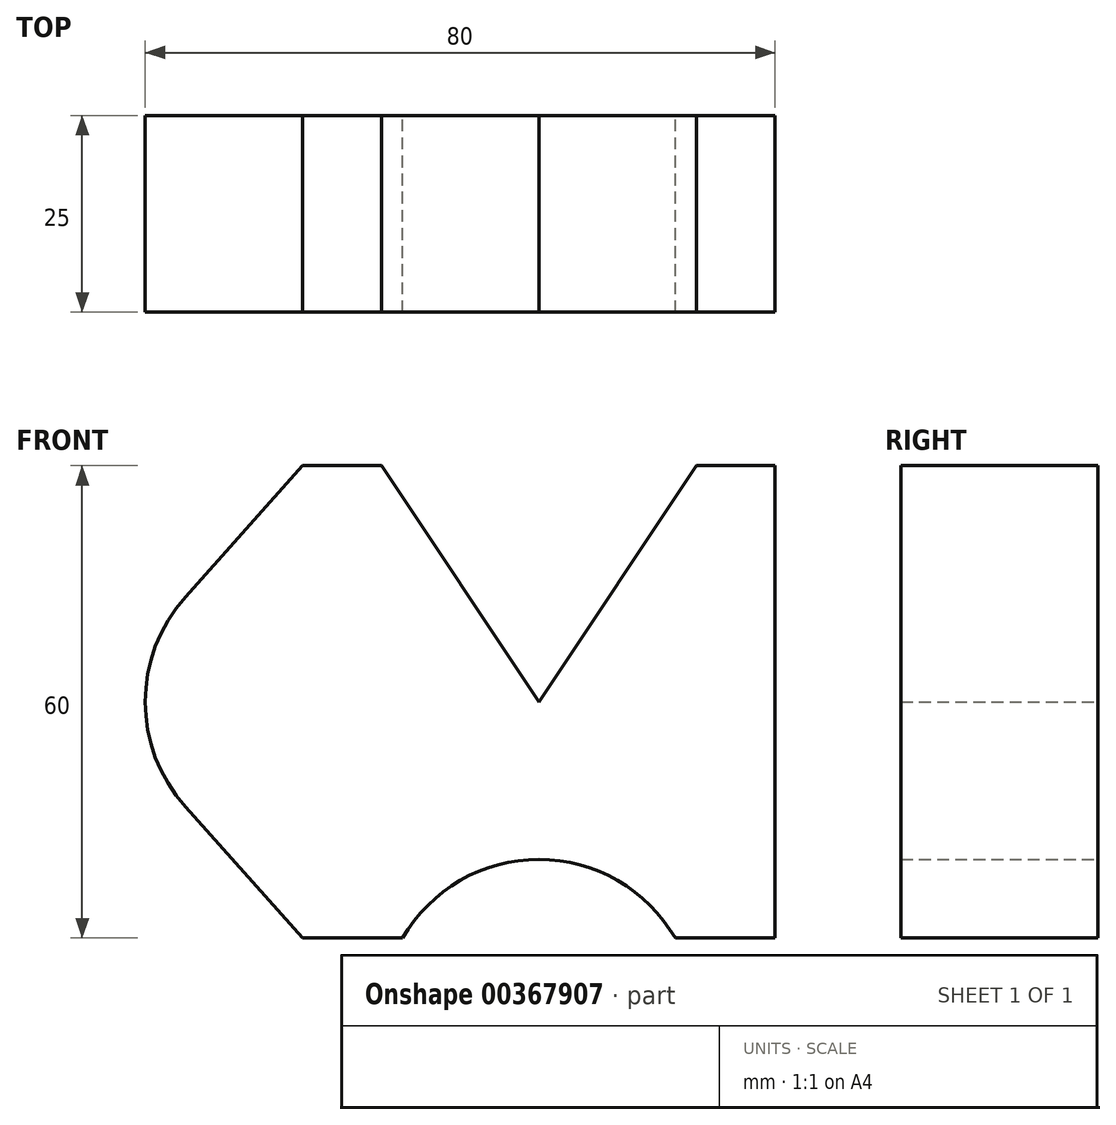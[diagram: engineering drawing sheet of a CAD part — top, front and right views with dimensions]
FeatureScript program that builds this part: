
annotation { "Feature Type Name" : "Feature", "Feature Type Description" : "" }
export const myFeature = defineFeature(function(context is Context, id is Id, definition is map)
    precondition{}
    {
        {
            var Q0;
            Q0=qCreatedBy(makeId("Front.planeOp"),FACE);
            var sketch = newSketch(context, id + "F0", { "sketchPlane" : qUnion([Q0])});
            skLineSegment(sketch, "E0", {"start": v(0, 0) * mm, "end": v(20, 30) * mm});
            skLineSegment(sketch, "E1", {"start": v(20, 30) * mm, "end": v(30, 30) * mm});
            skLineSegment(sketch, "E2", {"start": v(30, 30) * mm, "end": v(30, -30) * mm});
            skLineSegment(sketch, "E3", {"start": v(30, -30) * mm, "end": v(17.32, -30) * mm});
            skArc(sketch, "E4", {"start": v(17.32, -30) * mm, "mid": v(0, -20) * mm, "end": v(-17.32, -30) * mm});
            skLineSegment(sketch, "E5", {"start": v(-30, 30) * mm, "end": v(-20, 30) * mm});
            skLineSegment(sketch, "E6", {"start": v(-20, 30) * mm, "end": v(0, 0) * mm});
            skLineSegment(sketch, "E7", {"start": v(-17.32, -30) * mm, "end": v(-30, -30) * mm});
            skLineSegment(sketch, "E8", {"start": v(-30, -30) * mm, "end": v(-44.9, -13.33) * mm});
            skArc(sketch, "E9", {"start": v(-44.9, 13.33) * mm, "mid": v(-50, 0) * mm, "end": v(-44.9, -13.33) * mm});
            skLineSegment(sketch, "E10", {"start": v(-44.9, 13.33) * mm, "end": v(-30, 30) * mm});
            skLineSegment(sketch, "E11", {"start": v(-30, 30) * mm, "end": v(-30, -62.87) * mm, "construction": true});
            skSolve(sketch);
        }
        {
            var Q0;
            Q0=makeQuery(id+"F0.imprint","IMPRINT",FACE,{"disambiguationData":[TD([[makeQuery(id+"F0.imprint","IMPRINT",EDGE,{"derivedFrom":sQuery(id+"F0.wireOp",EDGE,"E0")}),-1.0]])]});
            extrude(context, id + "F1", {"entities" : qUnion([Q0]), "depth" : 25 * mm});
        }
    });
